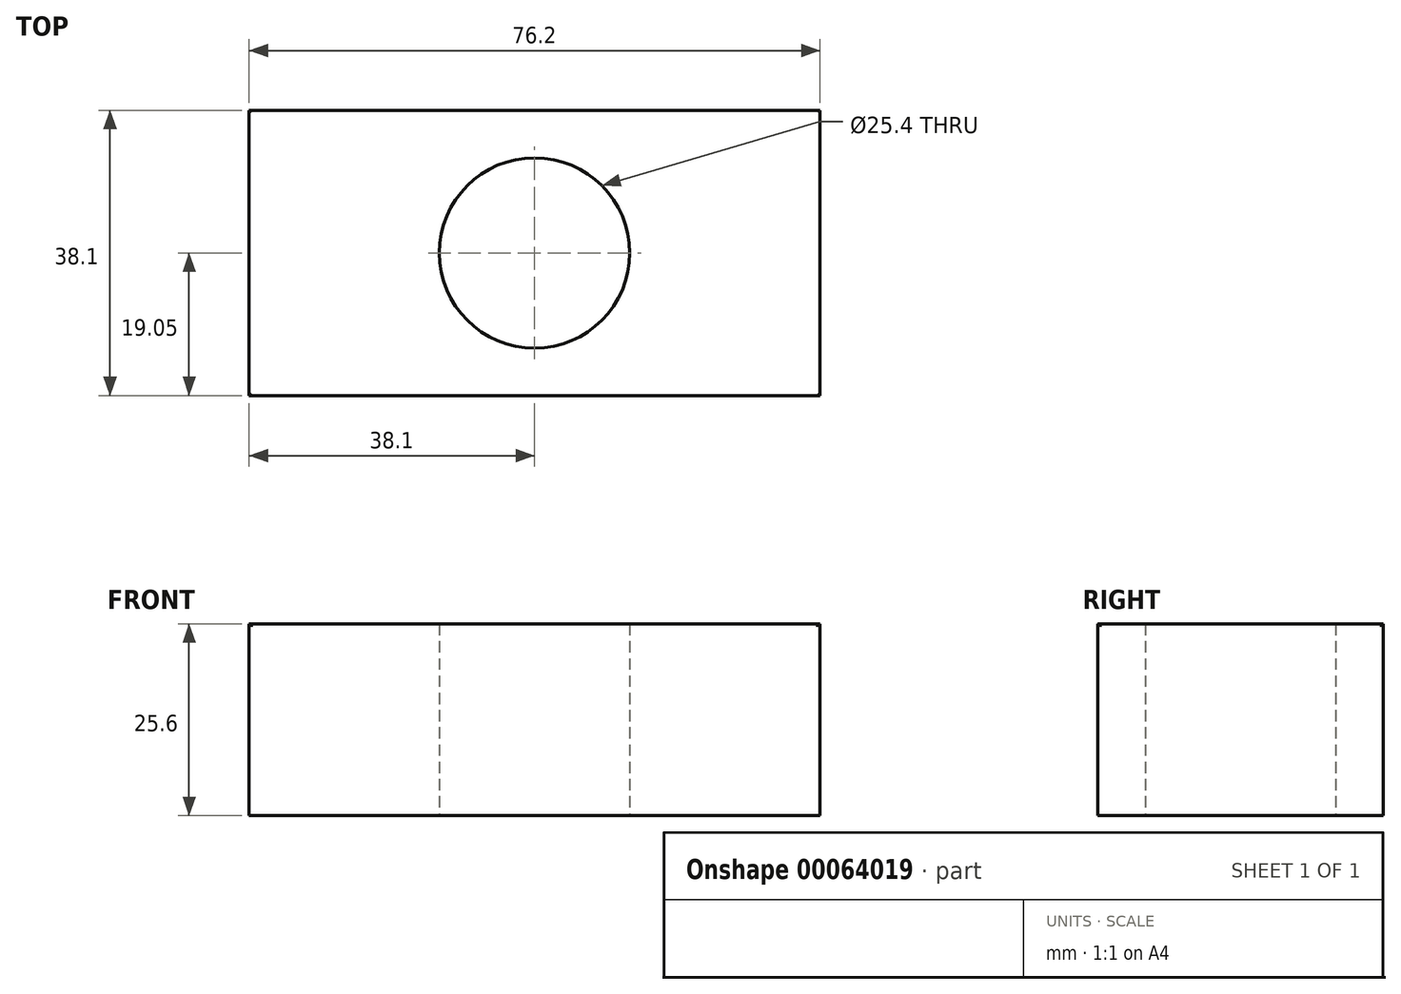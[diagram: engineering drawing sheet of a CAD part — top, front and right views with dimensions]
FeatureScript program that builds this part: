
annotation { "Feature Type Name" : "Feature", "Feature Type Description" : "" }
export const myFeature = defineFeature(function(context is Context, id is Id, definition is map)
    precondition{}
    {
        {
            assignVariable(context, id + "F0", {"name" : "d", "anyValue" : 1});
        }
        {
            var Q0;
            Q0=qCreatedBy(makeId("Top.planeOp"),FACE);
            var sketch = newSketch(context, id + "F1", { "sketchPlane" : qUnion([Q0])});
            skLineSegment(sketch, "E0.bottom", {"start": v(-38.1, 19.05) * mm, "end": v(38.1, 19.05) * mm});
            skLineSegment(sketch, "E0.top", {"start": v(-38.1, -19.05) * mm, "end": v(38.1, -19.05) * mm});
            skLineSegment(sketch, "E0.left", {"start": v(-38.1, 19.05) * mm, "end": v(-38.1, -19.05) * mm});
            skLineSegment(sketch, "E0.right", {"start": v(38.1, 19.05) * mm, "end": v(38.1, -19.05) * mm});
            skCircle(sketch, "E1", {"center": v(0, 0) * mm, "radius": 12.7 * mm});
            skSolve(sketch);
        }
        {
            var Q0;
            Q0 = qSketchRegion(id + "F1", true);
            extrude(context, id + "F2", {"entities" : qUnion([Q0]), "depth" : (getVariable(context, 'd') * .2) * mm});
        }
        {
            var Q0;
            Q0=makeQuery(id+"F2.opExtrude","SWEPT_EDGE",EDGE,{"disambiguationData":[OSD([sQuery(id+"F1.wireOp",EDGE,"E0.top"),sQuery(id+"F1.wireOp",EDGE,"E0.right")])]});
            var Q1;
            Q1=makeQuery(id+"F2.opExtrude","SWEPT_EDGE",EDGE,{"disambiguationData":[OSD([sQuery(id+"F1.wireOp",EDGE,"E0.bottom"),sQuery(id+"F1.wireOp",EDGE,"E0.right")])]});
            var Q2;
            Q2=makeQuery(id+"F2.opExtrude","SWEPT_EDGE",EDGE,{"disambiguationData":[OSD([sQuery(id+"F1.wireOp",EDGE,"E0.top"),sQuery(id+"F1.wireOp",EDGE,"E0.left")])]});
            var Q3;
            Q3=makeQuery(id+"F2.opExtrude","SWEPT_EDGE",EDGE,{"disambiguationData":[OSD([sQuery(id+"F1.wireOp",EDGE,"E0.bottom"),sQuery(id+"F1.wireOp",EDGE,"E0.left")])]});
            fillet(context, id + "F3", {"entities" : qUnion([Q0, Q1, Q2, Q3]), "radius" : (getVariable(context, 'd') / 2) * mm, "tangentPropagation" : true, "allowEdgeOverflow" : false});
        }
        {
            var Q0;
            Q0 = qSketchRegion(id + "F1", true);
            extrude(context, id + "F4", {"entities" : qUnion([Q0]), "operationType" : NewBodyOperationType.ADD, "oppositeDirection" : true, "depth" : 25.4 * mm});
        }
    });
